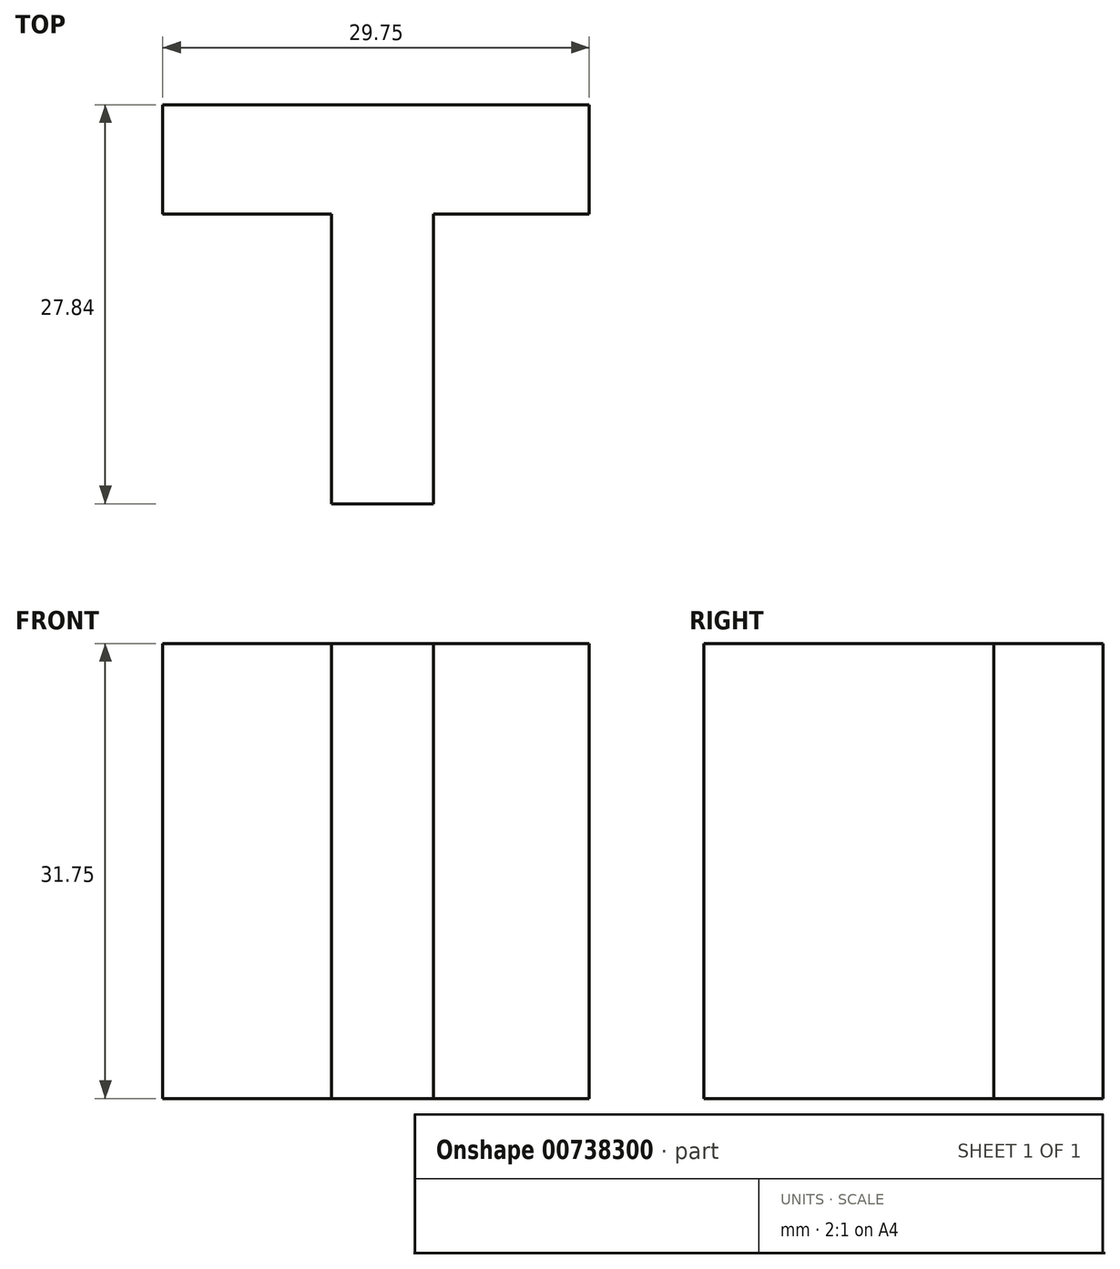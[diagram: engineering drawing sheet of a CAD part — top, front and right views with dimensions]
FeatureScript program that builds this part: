
annotation { "Feature Type Name" : "Feature", "Feature Type Description" : "" }
export const myFeature = defineFeature(function(context is Context, id is Id, definition is map)
    precondition{}
    {
        {
            var Q0;
            Q0=qCreatedBy(makeId("Top.planeOp"),FACE);
            var sketch = newSketch(context, id + "F0", { "sketchPlane" : qUnion([Q0])});
            skLineSegment(sketch, "E0", {"start": v(0, 0) * mm, "end": v(0, 20.2) * mm});
            skLineSegment(sketch, "E1", {"start": v(0, 20.2) * mm, "end": v(-11.76, 20.2) * mm});
            skLineSegment(sketch, "E2", {"start": v(-11.76, 20.2) * mm, "end": v(-11.76, 27.84) * mm});
            skLineSegment(sketch, "E3", {"start": v(-11.76, 27.84) * mm, "end": v(18, 27.84) * mm});
            skLineSegment(sketch, "E4", {"start": v(18, 27.84) * mm, "end": v(18, 20.2) * mm});
            skLineSegment(sketch, "E5", {"start": v(18, 20.2) * mm, "end": v(7.14, 20.2) * mm});
            skLineSegment(sketch, "E6", {"start": v(7.14, 20.2) * mm, "end": v(7.14, 0) * mm});
            skLineSegment(sketch, "E7", {"start": v(7.14, 0) * mm, "end": v(0, 0) * mm});
            skSolve(sketch);
        }
        {
            var Q0;
            Q0=makeQuery(id+"F0.imprint","IMPRINT",FACE,{"disambiguationData":[TD([[makeQuery(id+"F0.imprint","IMPRINT",EDGE,{"derivedFrom":sQuery(id+"F0.wireOp",EDGE,"E0")}),-1.0]])]});
            extrude(context, id + "F1", {"entities" : qUnion([Q0]), "depth" : 31.75 * mm, "offsetDistance" : 25.4 * mm});
        }
    });
